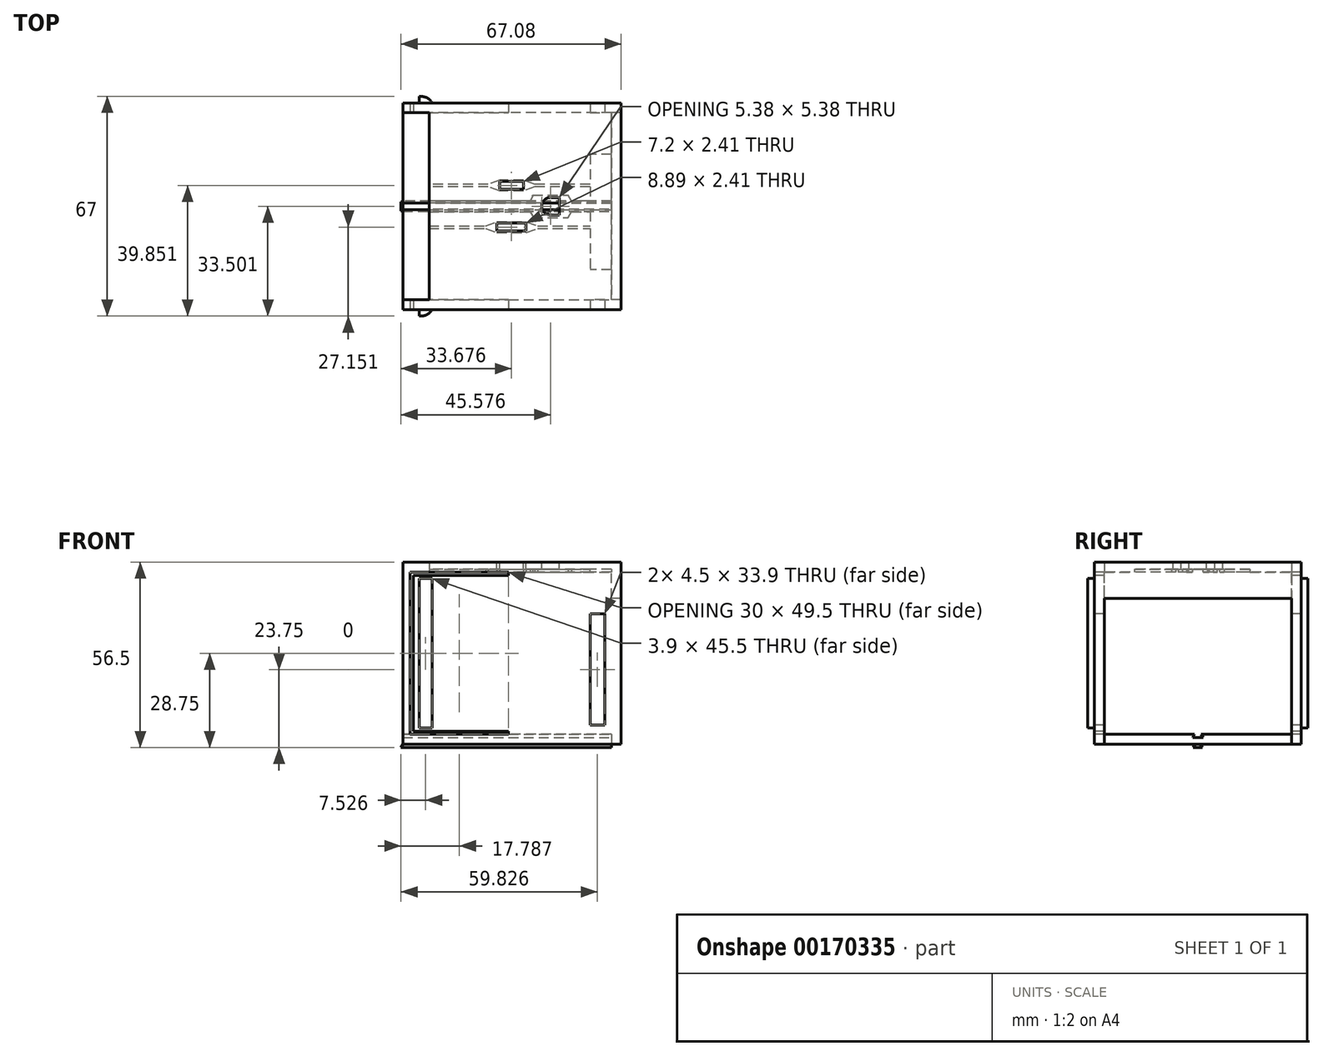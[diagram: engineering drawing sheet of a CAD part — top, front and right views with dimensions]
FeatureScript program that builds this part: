
annotation { "Feature Type Name" : "Feature", "Feature Type Description" : "" }
export const myFeature = defineFeature(function(context is Context, id is Id, definition is map)
    precondition{}
    {
        {
            var Q0;
            Q0=qCreatedBy(makeId("Top.planeOp"),FACE);
            var sketch = newSketch(context, id + "F0", { "sketchPlane" : qUnion([Q0])});
            skLineSegment(sketch, "E0", {"start": v(-33.77, 29.66) * mm, "end": v(-33.77, -33.34) * mm});
            skLineSegment(sketch, "E1", {"start": v(-33.77, -33.34) * mm, "end": v(32.73, -33.34) * mm});
            skLineSegment(sketch, "E2", {"start": v(32.73, -33.34) * mm, "end": v(32.73, 29.66) * mm});
            skLineSegment(sketch, "E3", {"start": v(32.73, 29.66) * mm, "end": v(-33.77, 29.66) * mm});
            skSolve(sketch);
        }
        {
            var Q0;
            Q0=makeQuery(id+"F0.imprint","IMPRINT",FACE,{"disambiguationData":[TD([[makeQuery(id+"F0.imprint","IMPRINT",EDGE,{"derivedFrom":sQuery(id+"F0.wireOp",EDGE,"E0")}),1.0]])]});
            extrude(context, id + "F1", {"entities" : qUnion([Q0]), "depth" : 55.5 * mm});
        }
        {
            var Q0;
            Q0=makeQuery(id+"F1.opExtrude","SWEPT_FACE",FACE,{"disambiguationData":[OSD([sQuery(id+"F0.wireOp",EDGE,"E2")])]});
            shell(context, id + "F2", {"entities" : qUnion([Q0]), "thickness" : 3 * mm});
        }
        {
            var Q0;
            Q0=makeQuery(id+"F2.opShell","OFFSET_FACE",FACE,{"disambiguationData":[OSD([sQuery(id+"F0.wireOp",EDGE,"E0")])]});
            var sketch = newSketch(context, id + "F3", { "sketchPlane" : qUnion([Q0])});
            skLineSegment(sketch, "E4.bottom", {"start": v(-30.34, 52.5) * mm, "end": v(26.66, 52.5) * mm});
            skLineSegment(sketch, "E4.top", {"start": v(-30.34, 3) * mm, "end": v(26.66, 3) * mm});
            skLineSegment(sketch, "E4.left", {"start": v(-30.34, 52.5) * mm, "end": v(-30.34, 3) * mm});
            skLineSegment(sketch, "E4.right", {"start": v(26.66, 52.5) * mm, "end": v(26.66, 3) * mm});
            skSolve(sketch);
        }
        {
            var Q0;
            Q0 = qSketchRegion(id + "F3", true);
            extrude(context, id + "F4", {"entities" : qUnion([Q0]), "operationType" : NewBodyOperationType.REMOVE, "oppositeDirection" : true, "depth" : 66.04 * mm});
        }
        {
            var Q0;
            {var subQ0=sQuery(id+"F0.wireOp",EDGE,"E3");var subQ1=sQuery(id+"F0.wireOp",EDGE,"E2");var subQ2=sQuery(id+"F0.wireOp",EDGE,"E1");var subQ3=sQuery(id+"F0.wireOp",EDGE,"E0");Q0=makeQuery(id+"F4.boolean.opBoolean","MERGE",FACE,{"derivedFrom":[makeQuery(id+"F2.opShell","OFFSET_FACE",FACE,{"disambiguationData":[OSD([subQ3,subQ2,subQ1,subQ0]),TDD([makeQuery(id+"F1.opExtrude","CAP_FACE",FACE,{"disambiguationData":[OSD([subQ3,subQ2,subQ1,subQ0])],"isStart":false})])]}),makeQuery(id+"F4.opExtrude","SWEPT_FACE",FACE,{"disambiguationData":[OSD([sQuery(id+"F3.wireOp",EDGE,"E4.bottom")])]})]});}
            var sketch = newSketch(context, id + "F5", { "sketchPlane" : qUnion([Q0])});
            skLineSegment(sketch, "E5.bottom", {"start": v(32.73, 30.34) * mm, "end": v(29.73, 30.34) * mm});
            skLineSegment(sketch, "E5.top", {"start": v(32.73, -26.66) * mm, "end": v(29.73, -26.66) * mm});
            skLineSegment(sketch, "E5.left", {"start": v(32.73, 30.34) * mm, "end": v(32.73, -26.66) * mm});
            skLineSegment(sketch, "E5.right", {"start": v(29.73, 30.34) * mm, "end": v(29.73, -26.66) * mm});
            skSolve(sketch);
        }
        {
            var Q0;
            Q0=makeQuery(id+"F5.imprint","IMPRINT",FACE,{"disambiguationData":[TD([[makeQuery(id+"F5.imprint","IMPRINT",EDGE,{"derivedFrom":sQuery(id+"F5.wireOp",EDGE,"E5.bottom")}),-1.0]])]});
            extrude(context, id + "F6", {"entities" : qUnion([Q0]), "operationType" : NewBodyOperationType.ADD, "depth" : 8 * mm});
        }
        {
            var Q0;
            Q0=makeQuery(id+"F1.opExtrude","CAP_FACE",FACE,{"disambiguationData":[OSD([sQuery(id+"F0.wireOp",EDGE,"E0"),sQuery(id+"F0.wireOp",EDGE,"E1"),sQuery(id+"F0.wireOp",EDGE,"E2"),sQuery(id+"F0.wireOp",EDGE,"E3")])],"isStart":false});
            var sketch = newSketch(context, id + "F7", { "sketchPlane" : qUnion([Q0])});
            skLineSegment(sketch, "E6.bottom", {"start": v(-5.12, -9.4) * mm, "end": v(3.77, -9.4) * mm});
            skLineSegment(sketch, "E6.top", {"start": v(-5.12, -6.98) * mm, "end": v(3.77, -6.98) * mm});
            skLineSegment(sketch, "E6.left", {"start": v(-5.12, -9.4) * mm, "end": v(-5.12, -6.98) * mm});
            skLineSegment(sketch, "E6.right", {"start": v(3.77, -9.4) * mm, "end": v(3.77, -6.98) * mm});
            skCircle(sketch, "E7", {"center": v(11.23, -1.84) * mm, "radius": 2.69 * mm});
            skLineSegment(sketch, "E8", {"start": v(11.23, -4.53) * mm, "end": v(13.92, -4.53) * mm});
            skLineSegment(sketch, "E9", {"start": v(13.92, -4.53) * mm, "end": v(13.92, 0.85) * mm});
            skLineSegment(sketch, "E10", {"start": v(13.92, 0.85) * mm, "end": v(11.23, 0.85) * mm});
            skLineSegment(sketch, "E11.bottom", {"start": v(-4.27, 3.3) * mm, "end": v(2.93, 3.3) * mm});
            skLineSegment(sketch, "E11.top", {"start": v(-4.27, 5.72) * mm, "end": v(2.93, 5.72) * mm});
            skLineSegment(sketch, "E11.left", {"start": v(-4.27, 3.3) * mm, "end": v(-4.27, 5.72) * mm});
            skLineSegment(sketch, "E11.right", {"start": v(2.93, 3.3) * mm, "end": v(2.93, 5.72) * mm});
            skSolve(sketch);
        }
        {
            var Q0;
            Q0=makeQuery(id+"F7.imprint","IMPRINT",FACE,{"disambiguationData":[TD([[makeQuery(id+"F7.imprint","IMPRINT",EDGE,{"derivedFrom":sQuery(id+"F7.wireOp",EDGE,"e5bbfb99-4a67-4e68-9260-14264c8d8d9f.bottom")}),1.0]])]});
            var Q1;
            Q1=makeQuery(id+"F7.imprint","IMPRINT",FACE,{"disambiguationData":[TD([[makeQuery(id+"F7.imprint","IMPRINT",EDGE,{"derivedFrom":sQuery(id+"F7.wireOp",EDGE,"748e32bf-3e21-4c84-b203-d0ab9b07700e.bottom")}),1.0]])]});
            var Q2;
            {var subQ0=sQuery(id+"F7.wireOp",EDGE,"2b9a5541-25b8-4ab9-8f51-0d6340bffa77");var subQ1=makeQuery(id+"F7.imprint","INTERSECT",VERTEX,{"derivedFrom":[subQ0,sQuery(id+"F7.wireOp",EDGE,"3faf525a-4cc9-4e1e-b277-8db2a83e1c23")]});Q2=makeQuery(id+"F7.imprint","IMPRINT",FACE,{"disambiguationData":[TD([[makeQuery(id+"F7.imprint","IMPRINT",EDGE,{"disambiguationData":[TD([[subQ1,1.0]])],"derivedFrom":subQ0}),1.0]])]});}
            var Q3;
            {var subQ0=sQuery(id+"F7.wireOp",EDGE,"3faf525a-4cc9-4e1e-b277-8db2a83e1c23");Q3=makeQuery(id+"F7.imprint","IMPRINT",FACE,{"disambiguationData":[TD([[makeQuery(id+"F7.imprint","IMPRINT",EDGE,{"derivedFrom":subQ0}),1.0]])]});}
            var Q4;
            Q4=makeQuery(id+"F7.imprint","IMPRINT",FACE,{"disambiguationData":[TD([[makeQuery(id+"F7.imprint","IMPRINT",EDGE,{"derivedFrom":sQuery(id+"F7.wireOp",EDGE,"E6.bottom")}),1.0]])]});
            var Q5;
            Q5=makeQuery(id+"F7.imprint","IMPRINT",FACE,{"disambiguationData":[TD([[makeQuery(id+"F7.imprint","IMPRINT",EDGE,{"derivedFrom":sQuery(id+"F7.wireOp",EDGE,"E11.bottom")}),1.0]])]});
            var Q6;
            {var subQ0=sQuery(id+"F7.wireOp",EDGE,"E7");var subQ1=makeQuery(id+"F7.imprint","INTERSECT",VERTEX,{"derivedFrom":[subQ0,sQuery(id+"F7.wireOp",EDGE,"E10")]});Q6=makeQuery(id+"F7.imprint","IMPRINT",FACE,{"disambiguationData":[TD([[makeQuery(id+"F7.imprint","IMPRINT",EDGE,{"disambiguationData":[TD([[subQ1,1.0]])],"derivedFrom":subQ0}),1.0]])]});}
            var Q7;
            {var subQ0=sQuery(id+"F7.wireOp",EDGE,"E8");Q7=makeQuery(id+"F7.imprint","IMPRINT",FACE,{"disambiguationData":[TD([[makeQuery(id+"F7.imprint","IMPRINT",EDGE,{"derivedFrom":subQ0}),1.0]])]});}
            var Q8;
            {var subQ0=sQuery(id+"F7.wireOp",EDGE,"E10");Q8=makeQuery(id+"F7.imprint","IMPRINT",FACE,{"disambiguationData":[TD([[makeQuery(id+"F7.imprint","IMPRINT",EDGE,{"derivedFrom":subQ0}),1.0]])]});}
            extrude(context, id + "F8", {"entities" : qUnion([Q0, Q1, Q2, Q3, Q4, Q5, Q6, Q7, Q8]), "operationType" : NewBodyOperationType.REMOVE, "oppositeDirection" : true, "depth" : 25.4 * mm});
        }
        {
            var Q0;
            Q0=makeQuery(id+"F1.opExtrude","SWEPT_FACE",FACE,{"disambiguationData":[OSD([sQuery(id+"F0.wireOp",EDGE,"E3")])]});
            var sketch = newSketch(context, id + "F9", { "sketchPlane" : qUnion([Q0])});
            skLineSegment(sketch, "E12.bottom", {"start": v(28.77, 50.5) * mm, "end": v(24.87, 50.5) * mm});
            skLineSegment(sketch, "E12.top", {"start": v(28.77, 5) * mm, "end": v(24.87, 5) * mm});
            skLineSegment(sketch, "E12.left", {"start": v(28.77, 50.5) * mm, "end": v(28.77, 5) * mm});
            skLineSegment(sketch, "E12.right", {"start": v(24.87, 50.5) * mm, "end": v(24.87, 5) * mm});
            skSolve(sketch);
        }
        {
            var Q0;
            Q0=makeQuery(id+"F9.imprint","IMPRINT",FACE,{"disambiguationData":[TD([[makeQuery(id+"F9.imprint","IMPRINT",EDGE,{"derivedFrom":sQuery(id+"F9.wireOp",EDGE,"E12.bottom")}),1.0]])]});
            extrude(context, id + "F10", {"entities" : qUnion([Q0]), "operationType" : NewBodyOperationType.ADD, "depth" : 2 * mm});
        }
        {
            var Q0;
            Q0=makeQuery(id+"F10.opExtrude","CAP_EDGE",EDGE,{"disambiguationData":[OSD([sQuery(id+"F9.wireOp",EDGE,"E12.right")])],"isStart":false});
            fillet(context, id + "F11", {"entities" : qUnion([Q0]), "radius" : 3.8 * mm, "tangentPropagation" : true, "allowEdgeOverflow" : false});
        }
        {
            var Q0;
            Q0=makeQuery(id+"F1.opExtrude","SWEPT_FACE",FACE,{"disambiguationData":[OSD([sQuery(id+"F0.wireOp",EDGE,"E1")])]});
            var sketch = newSketch(context, id + "F12", { "sketchPlane" : qUnion([Q0])});
            skLineSegment(sketch, "E13.bottom", {"start": v(-24.87, 50.5) * mm, "end": v(-28.77, 50.5) * mm});
            skLineSegment(sketch, "E13.top", {"start": v(-24.87, 5) * mm, "end": v(-28.77, 5) * mm});
            skLineSegment(sketch, "E13.left", {"start": v(-24.87, 50.5) * mm, "end": v(-24.87, 5) * mm});
            skLineSegment(sketch, "E13.right", {"start": v(-28.77, 50.5) * mm, "end": v(-28.77, 5) * mm});
            skSolve(sketch);
        }
        {
            var Q0;
            Q0=makeQuery(id+"F12.imprint","IMPRINT",FACE,{"disambiguationData":[TD([[makeQuery(id+"F12.imprint","IMPRINT",EDGE,{"derivedFrom":sQuery(id+"F12.wireOp",EDGE,"E13.bottom")}),1.0]])]});
            extrude(context, id + "F13", {"entities" : qUnion([Q0]), "operationType" : NewBodyOperationType.ADD, "depth" : 2 * mm});
        }
        {
            var Q0;
            Q0=makeQuery(id+"F13.opExtrude","CAP_EDGE",EDGE,{"disambiguationData":[OSD([sQuery(id+"F12.wireOp",EDGE,"E13.left")])],"isStart":false});
            fillet(context, id + "F14", {"entities" : qUnion([Q0]), "radius" : 3.8 * mm, "tangentPropagation" : true, "allowEdgeOverflow" : false});
        }
        {
            var Q0;
            Q0=makeQuery(id+"F1.opExtrude","SWEPT_FACE",FACE,{"disambiguationData":[OSD([sQuery(id+"F0.wireOp",EDGE,"E1")])]});
            var sketch = newSketch(context, id + "F15", { "sketchPlane" : qUnion([Q0])});
            skLineSegment(sketch, "E14", {"start": v(-31.56, 52.5) * mm, "end": v(-1.56, 52.5) * mm});
            skLineSegment(sketch, "E15", {"start": v(-1.56, 52.5) * mm, "end": v(-1.56, 51.5) * mm});
            skLineSegment(sketch, "E16", {"start": v(-1.56, 51.5) * mm, "end": v(-30.56, 51.5) * mm});
            skLineSegment(sketch, "E17", {"start": v(-30.56, 51.5) * mm, "end": v(-30.56, 4) * mm});
            skLineSegment(sketch, "E18", {"start": v(-30.56, 4) * mm, "end": v(-1.56, 4) * mm});
            skLineSegment(sketch, "E19", {"start": v(-1.56, 4) * mm, "end": v(-1.56, 3) * mm});
            skLineSegment(sketch, "E20", {"start": v(-1.56, 3) * mm, "end": v(-31.56, 3) * mm});
            skLineSegment(sketch, "E21", {"start": v(-31.56, 3) * mm, "end": v(-31.56, 52.5) * mm});
            skSolve(sketch);
        }
        {
            var Q0;
            Q0=makeQuery(id+"F15.imprint","IMPRINT",FACE,{"disambiguationData":[TD([[makeQuery(id+"F15.imprint","IMPRINT",EDGE,{"derivedFrom":sQuery(id+"F15.wireOp",EDGE,"E14")}),-1.0]])]});
            extrude(context, id + "F16", {"entities" : qUnion([Q0]), "operationType" : NewBodyOperationType.REMOVE, "oppositeDirection" : true, "depth" : 66.04 * mm});
        }
        {
            var Q0;
            Q0=makeQuery(id+"F1.opExtrude","SWEPT_FACE",FACE,{"disambiguationData":[OSD([sQuery(id+"F0.wireOp",EDGE,"E1")])]});
            var sketch = newSketch(context, id + "F17", { "sketchPlane" : qUnion([Q0])});
            skLineSegment(sketch, "E22.bottom", {"start": v(23.23, 39.7) * mm, "end": v(27.73, 39.7) * mm});
            skLineSegment(sketch, "E22.top", {"start": v(23.23, 5.8) * mm, "end": v(27.73, 5.8) * mm});
            skLineSegment(sketch, "E22.left", {"start": v(23.23, 39.7) * mm, "end": v(23.23, 5.8) * mm});
            skLineSegment(sketch, "E22.right", {"start": v(27.73, 39.7) * mm, "end": v(27.73, 5.8) * mm});
            skSolve(sketch);
        }
        {
            var Q0;
            Q0 = qSketchRegion(id + "F17", true);
            extrude(context, id + "F18", {"entities" : qUnion([Q0]), "operationType" : NewBodyOperationType.REMOVE, "oppositeDirection" : true, "depth" : 76 * mm});
        }
        {
            var Q0;
            {var subQ0=sQuery(id+"F0.wireOp",EDGE,"E3");var subQ1=sQuery(id+"F0.wireOp",EDGE,"E2");var subQ2=sQuery(id+"F0.wireOp",EDGE,"E1");var subQ3=sQuery(id+"F0.wireOp",EDGE,"E0");Q0=makeQuery(id+"F4.boolean.opBoolean","MERGE",FACE,{"derivedFrom":[makeQuery(id+"F2.opShell","OFFSET_FACE",FACE,{"disambiguationData":[OSD([subQ3,subQ2,subQ1,subQ0]),TDD([makeQuery(id+"F1.opExtrude","CAP_FACE",FACE,{"disambiguationData":[OSD([subQ3,subQ2,subQ1,subQ0])],"isStart":false})])]}),makeQuery(id+"F4.opExtrude","SWEPT_FACE",FACE,{"disambiguationData":[OSD([sQuery(id+"F3.wireOp",EDGE,"E4.bottom")])]})]});}
            var sketch = newSketch(context, id + "F19", { "sketchPlane" : qUnion([Q0])});
            skLineSegment(sketch, "E23.bottom", {"start": v(-33.77, -26.66) * mm, "end": v(-25.77, -26.66) * mm});
            skLineSegment(sketch, "E23.top", {"start": v(-33.77, 30.34) * mm, "end": v(-25.77, 30.34) * mm});
            skLineSegment(sketch, "E23.left", {"start": v(-33.77, -26.66) * mm, "end": v(-33.77, 30.34) * mm});
            skLineSegment(sketch, "E23.right", {"start": v(-25.77, -26.66) * mm, "end": v(-25.77, 30.34) * mm});
            skSolve(sketch);
        }
        {
            var Q0;
            Q0=makeQuery(id+"F19.imprint","IMPRINT",FACE,{"disambiguationData":[TD([[makeQuery(id+"F19.imprint","IMPRINT",EDGE,{"derivedFrom":sQuery(id+"F19.wireOp",EDGE,"E23.bottom")}),-1.0]])]});
            extrude(context, id + "F20", {"entities" : qUnion([Q0]), "operationType" : NewBodyOperationType.REMOVE, "oppositeDirection" : true, "depth" : 11.43 * mm});
        }
        {
            var Q0;
            {var subQ0=sQuery(id+"F0.wireOp",EDGE,"E3");var subQ1=sQuery(id+"F0.wireOp",EDGE,"E2");var subQ2=sQuery(id+"F0.wireOp",EDGE,"E1");var subQ3=sQuery(id+"F0.wireOp",EDGE,"E0");Q0=makeQuery(id+"F16.boolean.opBoolean","MERGE",FACE,{"derivedFrom":[makeQuery(id+"F4.boolean.opBoolean","MERGE",FACE,{"derivedFrom":[makeQuery(id+"F2.opShell","OFFSET_FACE",FACE,{"disambiguationData":[OSD([subQ3,subQ2,subQ1,subQ0]),TDD([makeQuery(id+"F1.opExtrude","CAP_FACE",FACE,{"disambiguationData":[OSD([subQ3,subQ2,subQ1,subQ0])],"isStart":false})])]}),makeQuery(id+"F4.opExtrude","SWEPT_FACE",FACE,{"disambiguationData":[OSD([sQuery(id+"F3.wireOp",EDGE,"E4.bottom")])]})]}),makeQuery(id+"F16.opExtrude","SWEPT_FACE",FACE,{"disambiguationData":[OSD([sQuery(id+"F15.wireOp",EDGE,"E14")])]})]});}
            var sketch = newSketch(context, id + "F21", { "sketchPlane" : qUnion([Q0])});
            skLineSegment(sketch, "E24.bottom", {"start": v(29.73, -4.11) * mm, "end": v(29.73, -4.91) * mm});
            skLineSegment(sketch, "E24.top", {"start": v(-25.77, -4.11) * mm, "end": v(-25.77, -4.91) * mm});
            skLineSegment(sketch, "E25", {"start": v(6.44, -4.11) * mm, "end": v(2.93, -2.88) * mm});
            skLineSegment(sketch, "E26", {"start": v(2.93, -2.88) * mm, "end": v(-4.27, -2.88) * mm});
            skLineSegment(sketch, "E27", {"start": v(-4.27, -2.88) * mm, "end": v(-7.79, -4.11) * mm});
            skLineSegment(sketch, "E28", {"start": v(6.44, -4.91) * mm, "end": v(2.93, -6.14) * mm});
            skLineSegment(sketch, "E29", {"start": v(2.93, -6.14) * mm, "end": v(-4.27, -6.14) * mm});
            skLineSegment(sketch, "E30", {"start": v(-4.27, -6.14) * mm, "end": v(-7.79, -4.91) * mm});
            skLineSegment(sketch, "E31", {"start": v(29.73, -4.11) * mm, "end": v(6.44, -4.11) * mm});
            skLineSegment(sketch, "E32", {"start": v(-7.79, -4.11) * mm, "end": v(-25.77, -4.11) * mm});
            skLineSegment(sketch, "E33", {"start": v(29.73, -4.91) * mm, "end": v(6.44, -4.91) * mm});
            skLineSegment(sketch, "E34", {"start": v(-7.79, -4.91) * mm, "end": v(-25.77, -4.91) * mm});
            skSolve(sketch);
        }
        {
            var Q0;
            Q0=makeQuery(id+"F21.imprint","IMPRINT",FACE,{"disambiguationData":[TD([[makeQuery(id+"F21.imprint","IMPRINT",EDGE,{"derivedFrom":sQuery(id+"F21.wireOp",EDGE,"E24.bottom")}),-1.0]])]});
            extrude(context, id + "F22", {"entities" : qUnion([Q0]), "operationType" : NewBodyOperationType.REMOVE, "oppositeDirection" : true, "depth" : 0.8 * mm});
        }
        {
            var Q0;
            Q0=makeQuery(id+"F1.opExtrude","CAP_FACE",FACE,{"disambiguationData":[OSD([sQuery(id+"F0.wireOp",EDGE,"E0"),sQuery(id+"F0.wireOp",EDGE,"E1"),sQuery(id+"F0.wireOp",EDGE,"E2"),sQuery(id+"F0.wireOp",EDGE,"E3")])],"isStart":true});
            var sketch = newSketch(context, id + "F23", { "sketchPlane" : qUnion([Q0])});
            skLineSegment(sketch, "E35.bottom", {"start": v(-33.77, 2.64) * mm, "end": v(32.73, 2.64) * mm});
            skLineSegment(sketch, "E35.top", {"start": v(-33.77, 1.04) * mm, "end": v(32.73, 1.04) * mm});
            skLineSegment(sketch, "E35.left", {"start": v(-33.77, 2.64) * mm, "end": v(-33.77, 1.04) * mm});
            skLineSegment(sketch, "E35.right", {"start": v(32.73, 2.64) * mm, "end": v(32.73, 1.04) * mm});
            skSolve(sketch);
        }
        {
            var Q0;
            Q0=makeQuery(id+"F23.imprint","IMPRINT",FACE,{"disambiguationData":[TD([[makeQuery(id+"F23.imprint","IMPRINT",EDGE,{"derivedFrom":sQuery(id+"F23.wireOp",EDGE,"E35.bottom")}),-1.0]])]});
            extrude(context, id + "F24", {"entities" : qUnion([Q0]), "operationType" : NewBodyOperationType.ADD, "depth" : 1 * mm, "hasDraft" : true, "draftAngle" : 30 * degree});
        }
        {
            var Q0;
            {var subQ0=sQuery(id+"F0.wireOp",EDGE,"E3");var subQ1=sQuery(id+"F0.wireOp",EDGE,"E2");var subQ2=sQuery(id+"F0.wireOp",EDGE,"E1");var subQ3=sQuery(id+"F0.wireOp",EDGE,"E0");Q0=makeQuery(id+"F16.boolean.opBoolean","MERGE",FACE,{"derivedFrom":[makeQuery(id+"F4.boolean.opBoolean","MERGE",FACE,{"derivedFrom":[makeQuery(id+"F2.opShell","OFFSET_FACE",FACE,{"disambiguationData":[OSD([subQ3,subQ2,subQ1,subQ0]),TDD([makeQuery(id+"F1.opExtrude","CAP_FACE",FACE,{"disambiguationData":[OSD([subQ3,subQ2,subQ1,subQ0])],"isStart":true})])]}),makeQuery(id+"F4.opExtrude","SWEPT_FACE",FACE,{"disambiguationData":[OSD([sQuery(id+"F3.wireOp",EDGE,"E4.top")])]})]}),makeQuery(id+"F16.opExtrude","SWEPT_FACE",FACE,{"disambiguationData":[OSD([sQuery(id+"F15.wireOp",EDGE,"E20")])]})]});}
            var sketch = newSketch(context, id + "F25", { "sketchPlane" : qUnion([Q0])});
            skLineSegment(sketch, "E36.bottom", {"start": v(-33.77, -2.84) * mm, "end": v(32.73, -2.84) * mm});
            skLineSegment(sketch, "E36.top", {"start": v(-33.77, -0.84) * mm, "end": v(32.73, -0.84) * mm});
            skLineSegment(sketch, "E36.left", {"start": v(-33.77, -2.84) * mm, "end": v(-33.77, -0.84) * mm});
            skLineSegment(sketch, "E36.right", {"start": v(32.73, -2.84) * mm, "end": v(32.73, -0.84) * mm});
            skSolve(sketch);
        }
        {
            var Q0;
            Q0=makeQuery(id+"F25.imprint","IMPRINT",FACE,{"disambiguationData":[TD([[makeQuery(id+"F25.imprint","IMPRINT",EDGE,{"derivedFrom":sQuery(id+"F25.wireOp",EDGE,"E36.bottom")}),1.0]])]});
            extrude(context, id + "F26", {"entities" : qUnion([Q0]), "operationType" : NewBodyOperationType.REMOVE, "oppositeDirection" : true, "depth" : 1 * mm, "hasDraft" : true, "draftAngle" : 30 * degree});
        }
        {
            var Q0;
            {var subQ0=sQuery(id+"F0.wireOp",EDGE,"E1");var subQ1=makeQuery(id+"F1.opExtrude","SWEPT_FACE",FACE,{"disambiguationData":[OSD([subQ0])]});var subQ4=makeQuery(id+"F4.opExtrude","SWEPT_FACE",FACE,{"disambiguationData":[OSD([sQuery(id+"F3.wireOp",EDGE,"E4.bottom")])]});var subQ5=sQuery(id+"F0.wireOp",EDGE,"E3");var subQ6=sQuery(id+"F0.wireOp",EDGE,"E2");var subQ7=sQuery(id+"F0.wireOp",EDGE,"E0");var subQ8=makeQuery(id+"F2.opShell","OFFSET_FACE",FACE,{"disambiguationData":[OSD([subQ7,subQ0,subQ6,subQ5]),TDD([makeQuery(id+"F1.opExtrude","CAP_FACE",FACE,{"disambiguationData":[OSD([subQ7,subQ0,subQ6,subQ5])],"isStart":false})])]});var subQ9=makeQuery(id+"F16.opExtrude","SWEPT_FACE",FACE,{"disambiguationData":[OSD([sQuery(id+"F15.wireOp",EDGE,"E14")])]});Q0=makeQuery(id+"F22.boolean.opBoolean","SPLIT",FACE,{"disambiguationData":[TD([subQ1])],"derivedFrom":makeQuery(id+"F16.boolean.opBoolean","MERGE",FACE,{"derivedFrom":[makeQuery(id+"F4.boolean.opBoolean","MERGE",FACE,{"derivedFrom":[subQ8,subQ4]}),subQ9]})});}
            var sketch = newSketch(context, id + "F27", { "sketchPlane" : qUnion([Q0])});
            skLineSegment(sketch, "E37", {"start": v(-25.77, 0.19) * mm, "end": v(-25.77, 3.49) * mm});
            skLineSegment(sketch, "E38", {"start": v(-25.77, 3.49) * mm, "end": v(5.03, 3.49) * mm});
            skLineSegment(sketch, "E39", {"start": v(5.03, 3.49) * mm, "end": v(5.78, 4.79) * mm});
            skLineSegment(sketch, "E40", {"start": v(16.58, 5.29) * mm, "end": v(17.62, 3.49) * mm});
            skLineSegment(sketch, "E41", {"start": v(17.62, 3.49) * mm, "end": v(29.73, 3.49) * mm});
            skLineSegment(sketch, "E42", {"start": v(29.73, 3.49) * mm, "end": v(29.73, 0.19) * mm});
            skLineSegment(sketch, "E43", {"start": v(29.73, 0.19) * mm, "end": v(17.62, 0.19) * mm});
            skLineSegment(sketch, "E44", {"start": v(17.62, 0.19) * mm, "end": v(16.58, -1.61) * mm});
            skLineSegment(sketch, "E45", {"start": v(5.78, -1.11) * mm, "end": v(5.03, 0.19) * mm});
            skLineSegment(sketch, "E46", {"start": v(5.03, 0.19) * mm, "end": v(-25.77, 0.19) * mm});
            skLineSegment(sketch, "E47", {"start": v(5.78, 4.79) * mm, "end": v(5.78, 5.29) * mm});
            skLineSegment(sketch, "E48", {"start": v(5.78, 5.29) * mm, "end": v(16.58, 5.29) * mm});
            skLineSegment(sketch, "E49", {"start": v(16.58, 5.29) * mm, "end": v(16.58, 5.29) * mm});
            skLineSegment(sketch, "E50", {"start": v(5.78, -1.11) * mm, "end": v(5.78, -1.61) * mm});
            skLineSegment(sketch, "E51", {"start": v(5.78, -1.61) * mm, "end": v(16.58, -1.61) * mm});
            skLineSegment(sketch, "E52", {"start": v(16.58, -1.61) * mm, "end": v(16.58, -1.61) * mm});
            skSolve(sketch);
        }
        {
            var Q0;
            Q0=makeQuery(id+"F27.imprint","IMPRINT",FACE,{"disambiguationData":[TD([[makeQuery(id+"F27.imprint","IMPRINT",EDGE,{"derivedFrom":sQuery(id+"F27.wireOp",EDGE,"E37")}),-1.0]])]});
            extrude(context, id + "F28", {"entities" : qUnion([Q0]), "operationType" : NewBodyOperationType.REMOVE, "oppositeDirection" : true, "depth" : 0.8 * mm});
        }
        {
            var Q0;
            {var subQ1=sQuery(id+"F0.wireOp",EDGE,"E1");var subQ3=sQuery(id+"F0.wireOp",EDGE,"E3");var subQ4=sQuery(id+"F0.wireOp",EDGE,"E2");var subQ5=sQuery(id+"F0.wireOp",EDGE,"E0");var subQ6=makeQuery(id+"F2.opShell","OFFSET_FACE",FACE,{"disambiguationData":[OSD([subQ5,subQ1,subQ4,subQ3]),TDD([makeQuery(id+"F1.opExtrude","CAP_FACE",FACE,{"disambiguationData":[OSD([subQ5,subQ1,subQ4,subQ3])],"isStart":false})])]});var subQ7=makeQuery(id+"F4.opExtrude","SWEPT_FACE",FACE,{"disambiguationData":[OSD([sQuery(id+"F3.wireOp",EDGE,"E4.bottom")])]});var subQ8=makeQuery(id+"F1.opExtrude","SWEPT_FACE",FACE,{"disambiguationData":[OSD([subQ1])]});var subQ10=makeQuery(id+"F16.opExtrude","SWEPT_FACE",FACE,{"disambiguationData":[OSD([sQuery(id+"F15.wireOp",EDGE,"E14")])]});Q0=makeQuery(id+"F28.boolean.opBoolean","SPLIT",FACE,{"disambiguationData":[TD([subQ8])],"derivedFrom":makeQuery(id+"F22.boolean.opBoolean","SPLIT",FACE,{"disambiguationData":[TD([subQ8])],"derivedFrom":makeQuery(id+"F16.boolean.opBoolean","MERGE",FACE,{"derivedFrom":[makeQuery(id+"F4.boolean.opBoolean","MERGE",FACE,{"derivedFrom":[subQ6,subQ7]}),subQ10]})})});}
            var sketch = newSketch(context, id + "F29", { "sketchPlane" : qUnion([Q0])});
            skLineSegment(sketch, "E53.bottom", {"start": v(-25.77, 7.79) * mm, "end": v(-25.77, 8.59) * mm});
            skLineSegment(sketch, "E53.top", {"start": v(29.73, 7.79) * mm, "end": v(29.73, 8.59) * mm});
            skLineSegment(sketch, "E54", {"start": v(-8.63, 7.79) * mm, "end": v(-5.12, 6.56) * mm});
            skLineSegment(sketch, "E55", {"start": v(-5.12, 6.56) * mm, "end": v(3.77, 6.56) * mm});
            skLineSegment(sketch, "E56", {"start": v(3.77, 6.56) * mm, "end": v(7.28, 7.79) * mm});
            skLineSegment(sketch, "E57", {"start": v(-8.63, 8.59) * mm, "end": v(-5.12, 9.82) * mm});
            skLineSegment(sketch, "E58", {"start": v(-5.12, 9.82) * mm, "end": v(3.77, 9.82) * mm});
            skLineSegment(sketch, "E59", {"start": v(3.77, 9.82) * mm, "end": v(7.28, 8.59) * mm});
            skLineSegment(sketch, "E60", {"start": v(-25.77, 7.79) * mm, "end": v(-8.63, 7.79) * mm});
            skLineSegment(sketch, "E61", {"start": v(7.28, 7.79) * mm, "end": v(29.73, 7.79) * mm});
            skLineSegment(sketch, "E62", {"start": v(-25.77, 8.59) * mm, "end": v(-8.63, 8.59) * mm});
            skLineSegment(sketch, "E63", {"start": v(7.28, 8.59) * mm, "end": v(29.73, 8.59) * mm});
            skSolve(sketch);
        }
        {
            var Q0;
            Q0=makeQuery(id+"F29.imprint","IMPRINT",FACE,{"disambiguationData":[TD([[makeQuery(id+"F29.imprint","IMPRINT",EDGE,{"derivedFrom":sQuery(id+"F29.wireOp",EDGE,"E53.bottom")}),-1.0]])]});
            extrude(context, id + "F30", {"entities" : qUnion([Q0]), "operationType" : NewBodyOperationType.REMOVE, "oppositeDirection" : true, "depth" : 0.8 * mm});
        }
        {
            var Q0;
            {var subQ0=sQuery(id+"F0.wireOp",EDGE,"E3");var subQ1=makeQuery(id+"F1.opExtrude","SWEPT_FACE",FACE,{"disambiguationData":[OSD([subQ0])]});var subQ2=makeQuery(id+"F4.opExtrude","SWEPT_FACE",FACE,{"disambiguationData":[OSD([sQuery(id+"F3.wireOp",EDGE,"E4.bottom")])]});var subQ3=sQuery(id+"F0.wireOp",EDGE,"E2");var subQ4=sQuery(id+"F0.wireOp",EDGE,"E1");var subQ5=sQuery(id+"F0.wireOp",EDGE,"E0");var subQ6=makeQuery(id+"F2.opShell","OFFSET_FACE",FACE,{"disambiguationData":[OSD([subQ5,subQ4,subQ3,subQ0]),TDD([makeQuery(id+"F1.opExtrude","CAP_FACE",FACE,{"disambiguationData":[OSD([subQ5,subQ4,subQ3,subQ0])],"isStart":false})])]});var subQ9=makeQuery(id+"F16.opExtrude","SWEPT_FACE",FACE,{"disambiguationData":[OSD([sQuery(id+"F15.wireOp",EDGE,"E14")])]});Q0=makeQuery(id+"F22.boolean.opBoolean","SPLIT",FACE,{"disambiguationData":[TD([subQ1])],"derivedFrom":makeQuery(id+"F16.boolean.opBoolean","MERGE",FACE,{"derivedFrom":[makeQuery(id+"F4.boolean.opBoolean","MERGE",FACE,{"derivedFrom":[subQ6,subQ2]}),subQ9]})});}
            var sketch = newSketch(context, id + "F31", { "sketchPlane" : qUnion([Q0])});
            skLineSegment(sketch, "E64.bottom", {"start": v(29.73, -13.98) * mm, "end": v(23.23, -13.98) * mm});
            skLineSegment(sketch, "E64.top", {"start": v(29.73, 21.21) * mm, "end": v(23.23, 21.21) * mm});
            skLineSegment(sketch, "E64.left", {"start": v(29.73, -13.98) * mm, "end": v(29.73, 21.21) * mm});
            skLineSegment(sketch, "E64.right", {"start": v(23.23, -13.98) * mm, "end": v(23.23, 21.21) * mm});
            skSolve(sketch);
        }
        {
            var Q0;
            {var subQ0=sQuery(id+"F31.wireOp",EDGE,"E64.top");Q0=makeQuery(id+"F31.imprint","IMPRINT",FACE,{"disambiguationData":[TD([[makeQuery(id+"F31.imprint","IMPRINT",EDGE,{"derivedFrom":subQ0}),1.0]])]});}
            var Q1;
            {var subQ0=sQuery(id+"F31.wireOp",EDGE,"E64.bottom");Q1=makeQuery(id+"F31.imprint","IMPRINT",FACE,{"disambiguationData":[TD([[makeQuery(id+"F31.imprint","IMPRINT",EDGE,{"derivedFrom":subQ0}),-1.0]])]});}
            extrude(context, id + "F32", {"entities" : qUnion([Q0, Q1]), "operationType" : NewBodyOperationType.REMOVE, "oppositeDirection" : true, "depth" : 0.8 * mm});
        }
        {
            var Q0;
            {var subQ0=sQuery(id+"F0.wireOp",EDGE,"E3");var subQ1=sQuery(id+"F0.wireOp",EDGE,"E2");var subQ2=sQuery(id+"F0.wireOp",EDGE,"E0");Q0=makeQuery(id+"F24.boolean.opBoolean","SPLIT",FACE,{"disambiguationData":[TD([makeQuery(id+"F1.opExtrude","SWEPT_FACE",FACE,{"disambiguationData":[OSD([subQ0])]})])],"derivedFrom":makeQuery(id+"F1.opExtrude","CAP_FACE",FACE,{"disambiguationData":[OSD([subQ2,sQuery(id+"F0.wireOp",EDGE,"E1"),subQ1,subQ0])],"isStart":true})});}
            var sketch = newSketch(context, id + "F33", { "sketchPlane" : qUnion([Q0])});
            skLineSegment(sketch, "E65.bottom", {"start": v(32.73, 30.34) * mm, "end": v(29.73, 30.34) * mm});
            skLineSegment(sketch, "E65.top", {"start": v(32.73, -26.66) * mm, "end": v(29.73, -26.66) * mm});
            skLineSegment(sketch, "E65.left", {"start": v(32.73, 30.34) * mm, "end": v(32.73, -26.66) * mm});
            skLineSegment(sketch, "E65.right", {"start": v(29.73, 30.34) * mm, "end": v(29.73, -26.66) * mm});
            skSolve(sketch);
        }
        {
            var Q0;
            {var subQ0=sQuery(id+"F33.wireOp",EDGE,"E65.bottom");Q0=makeQuery(id+"F33.imprint","IMPRINT",FACE,{"disambiguationData":[TD([[makeQuery(id+"F33.imprint","IMPRINT",EDGE,{"derivedFrom":subQ0}),1.0]])]});}
            var Q1;
            {var subQ0=sQuery(id+"F33.wireOp",EDGE,"E65.top");Q1=makeQuery(id+"F33.imprint","IMPRINT",FACE,{"disambiguationData":[TD([[makeQuery(id+"F33.imprint","IMPRINT",EDGE,{"derivedFrom":subQ0}),-1.0]])]});}
            extrude(context, id + "F34", {"entities" : qUnion([Q0, Q1]), "operationType" : NewBodyOperationType.REMOVE, "oppositeDirection" : true, "depth" : 25 * mm});
        }
        {
            var Q0;
            Q0=makeQuery(id+"F24.opExtrude","CAP_FACE",FACE,{"disambiguationData":[OSD([sQuery(id+"F23.wireOp",EDGE,"E35.bottom"),sQuery(id+"F23.wireOp",EDGE,"E35.top"),sQuery(id+"F23.wireOp",EDGE,"E35.left"),sQuery(id+"F23.wireOp",EDGE,"E35.right")])],"isStart":false});
            var sketch = newSketch(context, id + "F35", { "sketchPlane" : qUnion([Q0])});
            skLineSegment(sketch, "E66.bottom", {"start": v(33.3, 0.46) * mm, "end": v(29.8, 0.46) * mm});
            skLineSegment(sketch, "E66.top", {"start": v(33.3, 3.22) * mm, "end": v(29.8, 3.22) * mm});
            skLineSegment(sketch, "E66.left", {"start": v(33.3, 0.46) * mm, "end": v(33.3, 3.22) * mm});
            skLineSegment(sketch, "E66.right", {"start": v(29.8, 0.46) * mm, "end": v(29.8, 3.22) * mm});
            skSolve(sketch);
        }
        {
            var Q0;
            Q0=makeQuery(id+"F35.imprint","IMPRINT",FACE,{"disambiguationData":[TD([[makeQuery(id+"F35.imprint","IMPRINT",EDGE,{"derivedFrom":sQuery(id+"F35.wireOp",EDGE,"E66.bottom")}),1.0]])]});
            extrude(context, id + "F36", {"entities" : qUnion([Q0]), "operationType" : NewBodyOperationType.REMOVE, "oppositeDirection" : true, "depth" : 25 * mm});
        }
    });
